# Revit family: E_Cable Tray Support_MEPcontent_OBO Bettermann_US5
name_source: partatom
category: Cable Tray Fittings
revit_build: Autodesk Revit MEP 2015 (Build: 20140606_1530(x64)
units: mm (PartAtom-declared; Revit-internal decimal feet)

## types (11) — shared parameters
Article Description = U support with welded head plate.
Depth = 75 mm
Description = U support with welded head plate.
EMCS Version = 2.0
ETIM Article Class = EC000082
Family Version = 10.14
Gray = Color RGB 189-187-185
IFCExportAs = IfcCableCarrierFittingType
IFCExportType = NOTDEFINED
MEPcontent Class = CABLE_TRAY_SUPPORT
Manufacturer = OBO BETTERMANN
Manufacturer URL = http://catalog4.obo-bettermann.com
Product Line = OBO BETTERMANN CableTrays
Revit Version = 2015
URL = www.stabiplan.com
Width 1 = 50 mm  [stored 0.164042 ft]

## per-type parameters (varying)
| type | GTIN | Height 1 | Manufacturer Art. No. |
| US 5 K 20 VA4301 | 4012196477135 | 200 mm  [stored 0.656168 ft] | 6341358 |
| US 5 K 30 VA4301 | 4012196644230 | 300 mm | 6341362 |
| US 5 K 40 VA4301 | 4012196350292 | 400 mm  [stored 1.31234 ft] | 6341366 |
| US 5 K 50 VA4301 | 4012196350414 | 500 mm  [stored 1.64042 ft] | 6341370 |
| US 5 K 60 VA4301 | 4012196350476 | 600 mm | 6341374 |
| US 5 K 70 VA4301 | 4012196350537 | 700 mm  [stored 2.29659 ft] | 6341378 |
| US 5 K 80 VA4301 | 4012196350599 | 800 mm  [stored 2.62467 ft] | 6341382 |
| US 5 K 90 VA4301 | 4012196624492 | 900 mm  [stored 2.95276 ft] | 6341386 |
| US 5 K 100VA4301 | 4012196350711 | 1000 mm  [stored 3.28084 ft] | 6341390 |
| US 5 K 110VA4301 | 4012196350773 | 1100 mm | 6341394 |
| US 5 K 120VA4301 | 4012196350834 | 1200 mm | 6341398 |

note: column(s) folded — value = type name in every type: Article Type, Model

note: [stored X ft] marks values corroborated as IEEE doubles in the binary element streams (Revit-internal decimal feet)

## geometry (parser evidence)
native form markers: Blend x4, Sweep x3
no freeform markers — native parametric forms only
